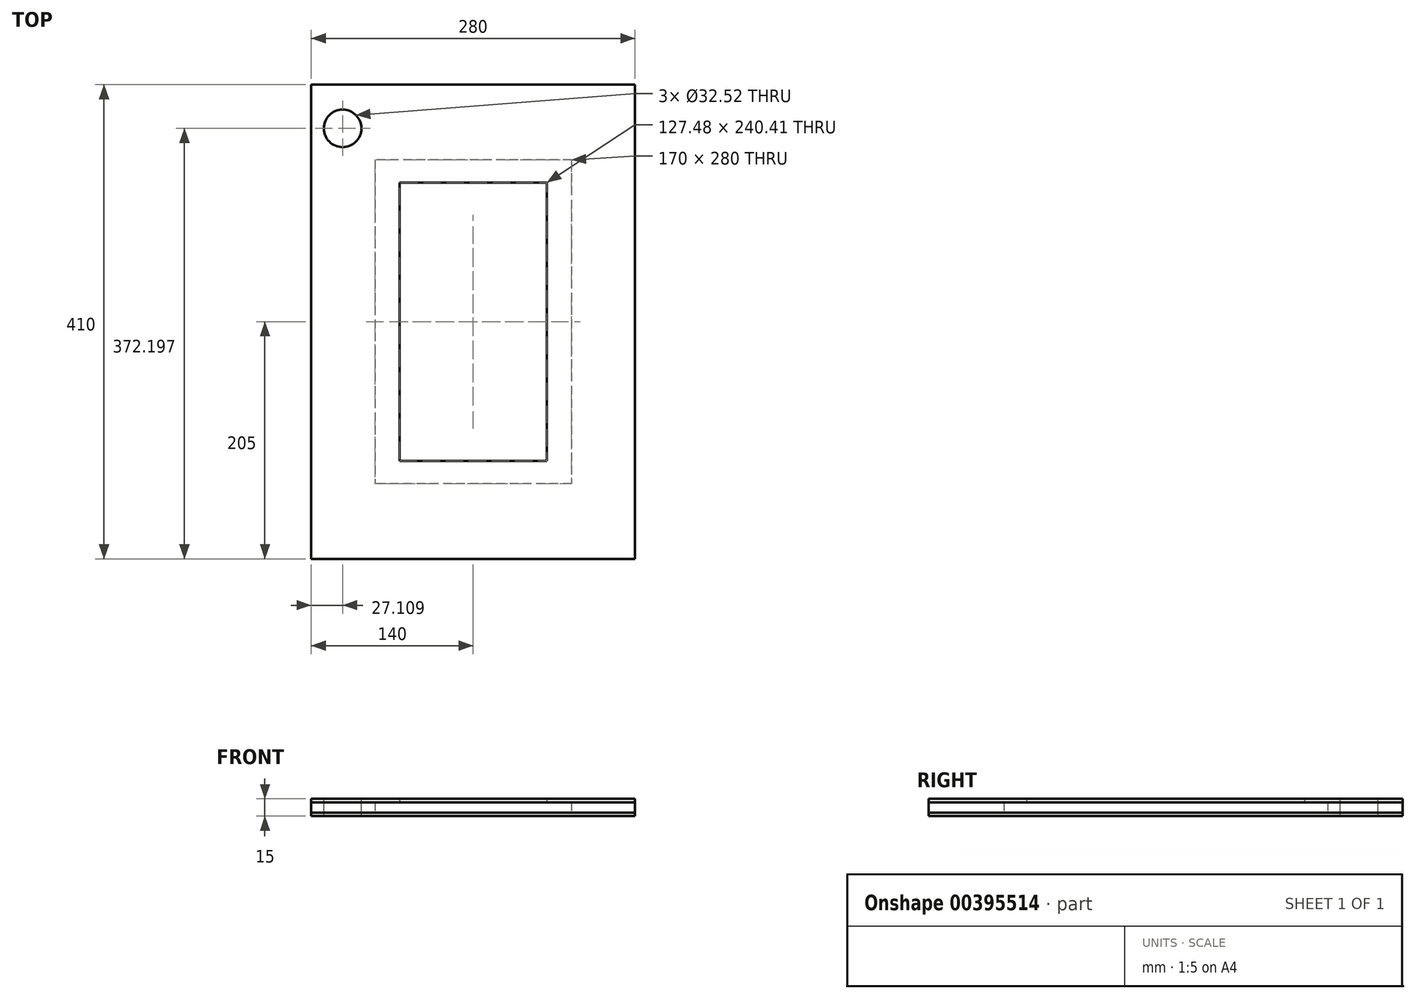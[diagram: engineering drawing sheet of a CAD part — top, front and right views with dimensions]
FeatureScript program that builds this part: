
annotation { "Feature Type Name" : "Feature", "Feature Type Description" : "" }
export const myFeature = defineFeature(function(context is Context, id is Id, definition is map)
    precondition{}
    {
        {
            var Q0;
            Q0=qCreatedBy(makeId("Top.planeOp"),FACE);
            var sketch = newSketch(context, id + "F0", { "sketchPlane" : qUnion([Q0])});
            skLineSegment(sketch, "E0.bottom", {"start": v(140, 205) * mm, "end": v(-140, 205) * mm});
            skLineSegment(sketch, "E0.top", {"start": v(140, -205) * mm, "end": v(-140, -205) * mm});
            skLineSegment(sketch, "E0.left", {"start": v(140, 205) * mm, "end": v(140, -205) * mm});
            skLineSegment(sketch, "E0.right", {"start": v(-140, 205) * mm, "end": v(-140, -205) * mm});
            skPoint(sketch, "E0.middle", {"position": v(0, 0) * mm});
            skSolve(sketch);
        }
        {
            var Q0;
            Q0 = qSketchRegion(id + "F0", true);
            extrude(context, id + "F1", {"entities" : qUnion([Q0]), "depth" : 3 * mm});
        }
        {
            var Q0;
            Q0=makeQuery(id+"F1.opExtrude","CAP_FACE",FACE,{"disambiguationData":[OSD([sQuery(id+"F0.wireOp",EDGE,"E0.bottom"),sQuery(id+"F0.wireOp",EDGE,"E0.top"),sQuery(id+"F0.wireOp",EDGE,"E0.left"),sQuery(id+"F0.wireOp",EDGE,"E0.right")])],"isStart":false});
            var sketch = newSketch(context, id + "F2", { "sketchPlane" : qUnion([Q0])});
            skLineSegment(sketch, "E1.bottom", {"start": v(-140, 205) * mm, "end": v(140, 205) * mm});
            skLineSegment(sketch, "E1.top", {"start": v(-140, -205) * mm, "end": v(140, -205) * mm});
            skLineSegment(sketch, "E1.left", {"start": v(-140, 205) * mm, "end": v(-140, -205) * mm});
            skLineSegment(sketch, "E1.right", {"start": v(140, 205) * mm, "end": v(140, -205) * mm});
            skLineSegment(sketch, "E2.bottom", {"start": v(85, 140) * mm, "end": v(-85, 140) * mm});
            skLineSegment(sketch, "E2.top", {"start": v(85, -140) * mm, "end": v(-85, -140) * mm});
            skLineSegment(sketch, "E2.left", {"start": v(85, 140) * mm, "end": v(85, -140) * mm});
            skLineSegment(sketch, "E2.right", {"start": v(-85, 140) * mm, "end": v(-85, -140) * mm});
            skPoint(sketch, "E2.middle", {"position": v(0, 0) * mm});
            skSolve(sketch);
        }
        {
            var Q0;
            Q0 = qSketchRegion(id + "F2", true);
            extrude(context, id + "F3", {"entities" : qUnion([Q0]), "depth" : 9 * mm});
        }
        {
            var Q0;
            Q0=makeQuery(id+"F3.opExtrude","CAP_FACE",FACE,{"disambiguationData":[OSD([sQuery(id+"F2.wireOp",EDGE,"E1.bottom"),sQuery(id+"F2.wireOp",EDGE,"E1.top"),sQuery(id+"F2.wireOp",EDGE,"E1.left"),sQuery(id+"F2.wireOp",EDGE,"E1.right"),sQuery(id+"F2.wireOp",EDGE,"E2.bottom"),sQuery(id+"F2.wireOp",EDGE,"E2.top"),sQuery(id+"F2.wireOp",EDGE,"E2.left"),sQuery(id+"F2.wireOp",EDGE,"E2.right")])],"isStart":false});
            var sketch = newSketch(context, id + "F4", { "sketchPlane" : qUnion([Q0])});
            skLineSegment(sketch, "E3.bottom", {"start": v(-140, 205) * mm, "end": v(140, 205) * mm});
            skLineSegment(sketch, "E3.top", {"start": v(-140, -205) * mm, "end": v(140, -205) * mm});
            skLineSegment(sketch, "E3.left", {"start": v(-140, 205) * mm, "end": v(-140, -205) * mm});
            skLineSegment(sketch, "E3.right", {"start": v(140, 205) * mm, "end": v(140, -205) * mm});
            skLineSegment(sketch, "E4.bottom", {"start": v(63.74, 120.2) * mm, "end": v(-63.74, 120.2) * mm});
            skLineSegment(sketch, "E4.top", {"start": v(63.74, -120.2) * mm, "end": v(-63.74, -120.2) * mm});
            skLineSegment(sketch, "E4.left", {"start": v(63.74, 120.2) * mm, "end": v(63.74, -120.2) * mm});
            skLineSegment(sketch, "E4.right", {"start": v(-63.74, 120.2) * mm, "end": v(-63.74, -120.2) * mm});
            skPoint(sketch, "E4.middle", {"position": v(0, 0) * mm});
            skSolve(sketch);
        }
        {
            var Q0;
            Q0 = qSketchRegion(id + "F4", true);
            extrude(context, id + "F5", {"entities" : qUnion([Q0]), "depth" : 3 * mm});
        }
        {
            var Q0;
            Q0=makeQuery(id+"F5.opExtrude","CAP_FACE",FACE,{"disambiguationData":[OSD([sQuery(id+"F4.wireOp",EDGE,"E3.bottom"),sQuery(id+"F4.wireOp",EDGE,"E3.top"),sQuery(id+"F4.wireOp",EDGE,"E3.left"),sQuery(id+"F4.wireOp",EDGE,"E3.right"),sQuery(id+"F4.wireOp",EDGE,"E4.bottom"),sQuery(id+"F4.wireOp",EDGE,"E4.top"),sQuery(id+"F4.wireOp",EDGE,"E4.left"),sQuery(id+"F4.wireOp",EDGE,"E4.right")])],"isStart":false});
            var sketch = newSketch(context, id + "F6", { "sketchPlane" : qUnion([Q0])});
            skCircle(sketch, "E5", {"center": v(-112.9, 167.2) * mm, "radius": 16.26 * mm});
            skSolve(sketch);
        }
        {
            var Q0;
            Q0 = qSketchRegion(id + "F6", true);
            extrude(context, id + "F7", {"entities" : qUnion([Q0]), "operationType" : NewBodyOperationType.REMOVE, "endBound" : BoundingType.THROUGH_ALL, "oppositeDirection" : true, "depth" : 25 * mm});
        }
    });
